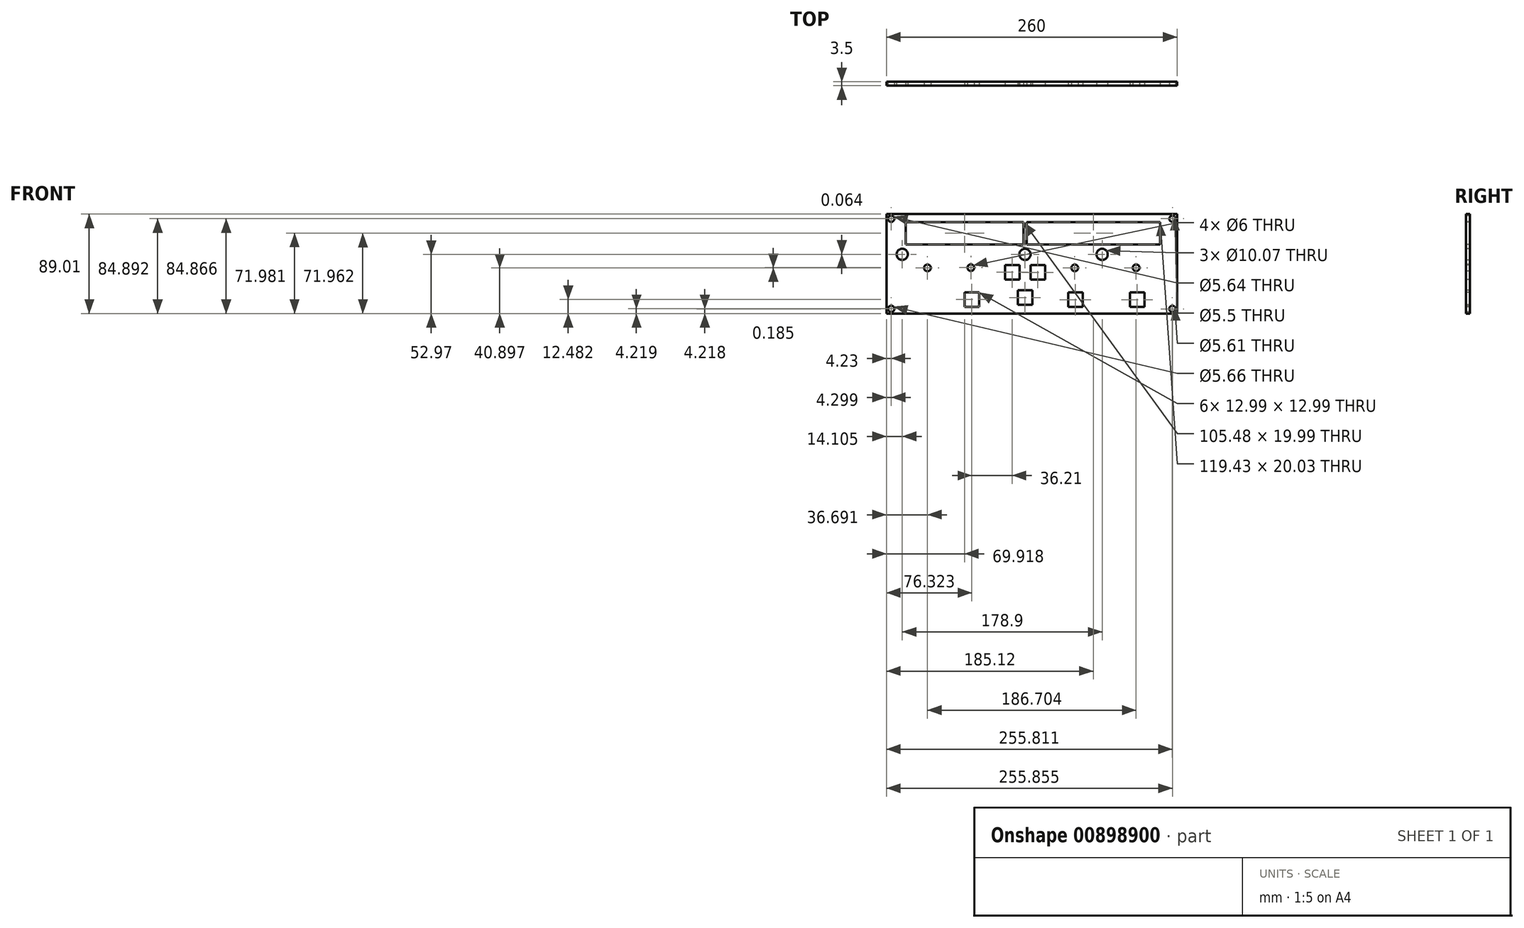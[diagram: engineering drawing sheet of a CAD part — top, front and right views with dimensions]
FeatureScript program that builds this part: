
annotation { "Feature Type Name" : "Feature", "Feature Type Description" : "" }
export const myFeature = defineFeature(function(context is Context, id is Id, definition is map)
    precondition{}
    {
        {
            var Q0;
            Q0=qCreatedBy(makeId("Front.planeOp"),FACE);
            var sketch = newSketch(context, id + "F0", { "sketchPlane" : qUnion([Q0])});
            skLineSegment(sketch, "E0.bottom", {"start": v(-123.83, 36.04) * mm, "end": v(136.17, 36.04) * mm});
            skLineSegment(sketch, "E0.top", {"start": v(-123.83, -52.97) * mm, "end": v(136.17, -52.97) * mm});
            skLineSegment(sketch, "E0.left", {"start": v(-123.83, 36.04) * mm, "end": v(-123.83, -52.97) * mm});
            skLineSegment(sketch, "E0.right", {"start": v(136.17, 36.04) * mm, "end": v(136.17, -52.97) * mm});
            skCircle(sketch, "E1", {"center": v(-119.6, 31.92) * mm, "radius": 2.82 * mm});
            skPoint(sketch, "E1.first.point", {"position": v(-121.7, 33.8) * mm});
            skPoint(sketch, "E1.second.point", {"position": v(-117.39, 33.67) * mm});
            skPoint(sketch, "E1.third.point", {"position": v(-119.56, 29.1) * mm});
            skCircle(sketch, "E2", {"center": v(132.03, 31.9) * mm, "radius": 2.75 * mm});
            skPoint(sketch, "E2.first.point", {"position": v(130, 33.75) * mm});
            skPoint(sketch, "E2.second.point", {"position": v(134.32, 33.4) * mm});
            skPoint(sketch, "E2.third.point", {"position": v(131.9, 29.15) * mm});
            skCircle(sketch, "E3", {"center": v(131.98, -48.75) * mm, "radius": 2.8 * mm});
            skPoint(sketch, "E3.first.point", {"position": v(129.91, -46.86) * mm});
            skPoint(sketch, "E3.second.point", {"position": v(134.24, -47.1) * mm});
            skPoint(sketch, "E3.third.point", {"position": v(131.88, -51.55) * mm});
            skCircle(sketch, "E4", {"center": v(-119.53, -48.75) * mm, "radius": 2.83 * mm});
            skPoint(sketch, "E4.first.point", {"position": v(-121.7, -46.94) * mm});
            skPoint(sketch, "E4.second.point", {"position": v(-117.39, -46.9) * mm});
            skPoint(sketch, "E4.third.point", {"position": v(-119.54, -51.58) * mm});
            skCircle(sketch, "E5", {"center": v(-109.72, 0.06) * mm, "radius": 5.04 * mm});
            skPoint(sketch, "E5.first.point", {"position": v(-113.21, 3.7) * mm});
            skPoint(sketch, "E5.second.point", {"position": v(-106.17, 3.63) * mm});
            skPoint(sketch, "E5.third.point", {"position": v(-109.3, -4.95) * mm});
            skCircle(sketch, "E6", {"center": v(-87.14, -12.07) * mm, "radius": 3 * mm});
            skPoint(sketch, "E6.first.point", {"position": v(-89.3, -10) * mm});
            skPoint(sketch, "E6.second.point", {"position": v(-85.02, -9.95) * mm});
            skPoint(sketch, "E6.third.point", {"position": v(-87.1, -15.07) * mm});
            skCircle(sketch, "E7", {"center": v(0.11, 0) * mm, "radius": 5.04 * mm});
            skCircle(sketch, "E8", {"center": v(69.18, 0) * mm, "radius": 5.04 * mm});
            skCircle(sketch, "E9", {"center": v(-48.31, -11.89) * mm, "radius": 3 * mm});
            skCircle(sketch, "E10", {"center": v(44.64, -12.06) * mm, "radius": 3 * mm});
            skCircle(sketch, "E11", {"center": v(99.56, -12.02) * mm, "radius": 3 * mm});
            skLineSegment(sketch, "E12.bottom", {"start": v(1.58, 29.02) * mm, "end": v(121, 29.02) * mm});
            skLineSegment(sketch, "E12.top", {"start": v(1.58, 9) * mm, "end": v(121, 9) * mm});
            skLineSegment(sketch, "E12.left", {"start": v(1.58, 29.02) * mm, "end": v(1.58, 9) * mm});
            skLineSegment(sketch, "E12.right", {"start": v(121, 29.02) * mm, "end": v(121, 9) * mm});
            skPoint(sketch, "E13.firstSnap0", {"position": v(61.3, 9) * mm});
            skLineSegment(sketch, "E13.bottom", {"start": v(-1.17, 9) * mm, "end": v(-106.65, 9) * mm});
            skLineSegment(sketch, "E13.top", {"start": v(-1.17, 28.99) * mm, "end": v(-106.65, 28.99) * mm});
            skLineSegment(sketch, "E13.left", {"start": v(-1.17, 9) * mm, "end": v(-1.17, 28.99) * mm});
            skLineSegment(sketch, "E13.right", {"start": v(-106.65, 9) * mm, "end": v(-106.65, 28.99) * mm});
            skLineSegment(sketch, "E14.bottom", {"start": v(-54, -34) * mm, "end": v(-41.01, -34) * mm});
            skLineSegment(sketch, "E14.top", {"start": v(-54, -46.98) * mm, "end": v(-41.01, -46.98) * mm});
            skLineSegment(sketch, "E14.left", {"start": v(-54, -34) * mm, "end": v(-54, -46.98) * mm});
            skLineSegment(sketch, "E14.right", {"start": v(-41.01, -34) * mm, "end": v(-41.01, -46.98) * mm});
            skLineSegment(sketch, "E15.bottom", {"start": v(-17.8, -9.53) * mm, "end": v(-4.8, -9.53) * mm});
            skLineSegment(sketch, "E15.top", {"start": v(-17.8, -22.52) * mm, "end": v(-4.8, -22.52) * mm});
            skLineSegment(sketch, "E15.left", {"start": v(-17.8, -9.53) * mm, "end": v(-17.8, -22.52) * mm});
            skLineSegment(sketch, "E15.right", {"start": v(-4.8, -9.53) * mm, "end": v(-4.8, -22.52) * mm});
            skLineSegment(sketch, "E16.bottom", {"start": v(5.12, -9.57) * mm, "end": v(18.1, -9.57) * mm});
            skLineSegment(sketch, "E16.top", {"start": v(5.12, -22.56) * mm, "end": v(18.1, -22.56) * mm});
            skLineSegment(sketch, "E16.left", {"start": v(5.12, -9.57) * mm, "end": v(5.12, -22.56) * mm});
            skLineSegment(sketch, "E16.right", {"start": v(18.1, -9.57) * mm, "end": v(18.1, -22.56) * mm});
            skLineSegment(sketch, "E17.bottom", {"start": v(-6.29, -32.22) * mm, "end": v(6.7, -32.22) * mm});
            skLineSegment(sketch, "E17.top", {"start": v(-6.29, -45.21) * mm, "end": v(6.7, -45.21) * mm});
            skLineSegment(sketch, "E17.left", {"start": v(-6.29, -32.22) * mm, "end": v(-6.29, -45.21) * mm});
            skLineSegment(sketch, "E17.right", {"start": v(6.7, -32.22) * mm, "end": v(6.7, -45.21) * mm});
            skLineSegment(sketch, "E18.bottom", {"start": v(38.79, -34.1) * mm, "end": v(51.78, -34.1) * mm});
            skLineSegment(sketch, "E18.top", {"start": v(38.79, -47.08) * mm, "end": v(51.78, -47.08) * mm});
            skLineSegment(sketch, "E18.left", {"start": v(38.79, -34.1) * mm, "end": v(38.79, -47.08) * mm});
            skLineSegment(sketch, "E18.right", {"start": v(51.78, -34.1) * mm, "end": v(51.78, -47.08) * mm});
            skLineSegment(sketch, "E19.bottom", {"start": v(94.02, -34.12) * mm, "end": v(107, -34.12) * mm});
            skLineSegment(sketch, "E19.top", {"start": v(94.02, -47.1) * mm, "end": v(107, -47.1) * mm});
            skLineSegment(sketch, "E19.left", {"start": v(94.02, -34.12) * mm, "end": v(94.02, -47.1) * mm});
            skLineSegment(sketch, "E19.right", {"start": v(107, -34.12) * mm, "end": v(107, -47.1) * mm});
            skSolve(sketch);
        }
        {
            var Q0;
            Q0=makeQuery(id+"F0.imprint","IMPRINT",FACE,{"disambiguationData":[TD([[makeQuery(id+"F0.imprint","IMPRINT",EDGE,{"derivedFrom":sQuery(id+"F0.wireOp",EDGE,"E0.bottom")}),-1.0]])]});
            extrude(context, id + "F1", {"entities" : qUnion([Q0]), "oppositeDirection" : true, "depth" : 3.5 * mm, "offsetDistance" : 25 * mm});
        }
    });
